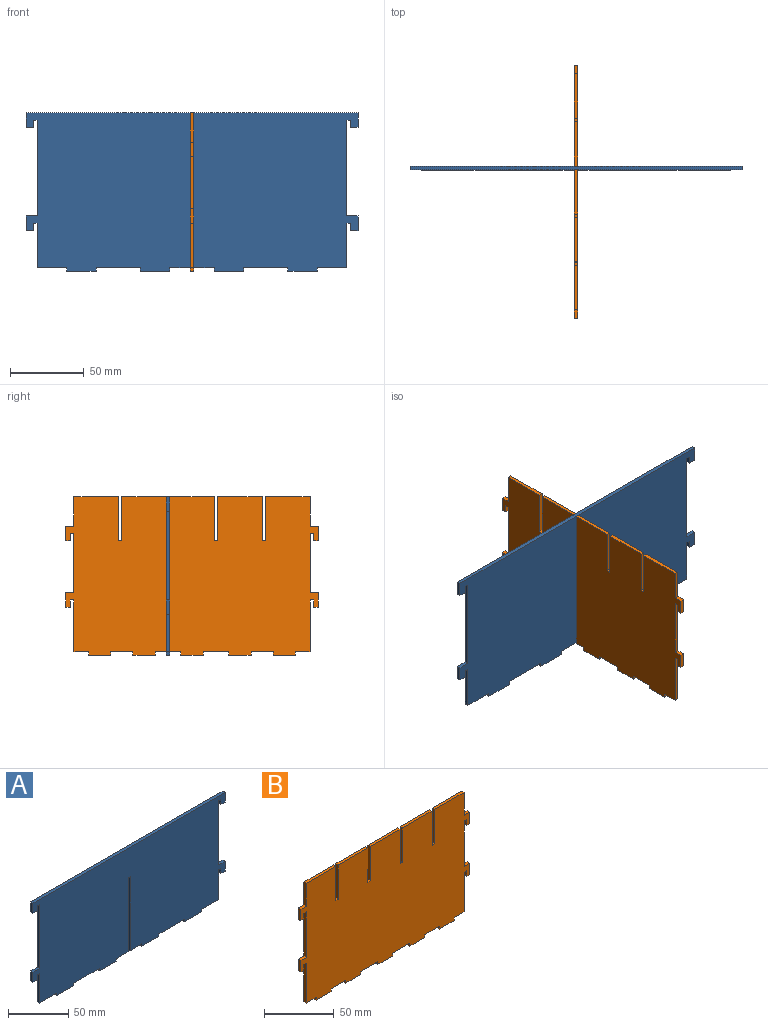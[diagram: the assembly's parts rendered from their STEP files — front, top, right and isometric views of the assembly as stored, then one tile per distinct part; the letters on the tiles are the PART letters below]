
ASSEMBLY  parts=2 mates=1
PART A: 46 faces, bbox 225x2.5x107.5 mm
  f0: plane 75x2.5mm, normal (1,0,0), area 187.5mm2, adj f1,f43,f44,f45
  f1: plane 2.5x2.5mm, normal (0,0,-1), area 6.2mm2, adj f0,f2,f44,f45
  f2: plane 75x2.5mm, normal (-1,0,0), area 187.5mm2, adj f1,f3,f44,f45
  f3: plane 13.75x2.5mm, normal (0,0,-1), area 34.4mm2, adj f2,f4,f44,f45
  f4: plane 2.5x2.5mm, normal (-1,0,0), area 6.2mm2, adj f3,f5,f44,f45
  f5: plane 20x2.5mm, normal (0,0,-1), area 50mm2, adj f4,f6,f44,f45
  f6: plane 2.5x2.5mm, normal (1,0,0), area 6.2mm2, adj f5,f7,f44,f45
  f7: plane 30x2.5mm, normal (0,0,-1), area 75mm2, adj f6,f8,f44,f45
  f8: plane 2.5x2.5mm, normal (-1,0,0), area 6.2mm2, adj f7,f9,f44,f45
  f9: plane 20x2.5mm, normal (0,0,-1), area 50mm2, adj f8,f10,f44,f45
  f10: plane 2.5x2.5mm, normal (1,0,0), area 6.2mm2, adj f9,f11,f44,f45
  f11: plane 20x2.5mm, normal (0,0,-1), area 50mm2, adj f10,f12,f44,f45
  f12: plane 30x2.5mm, normal (1,0,0), area 75mm2, adj f11,f13,f44,f45
  f13: plane 2.5x2.5mm, normal (0,0,-1), area 6.3mm2, adj f12,f14,f44,f45
  f14: plane 5x2.5mm, normal (-1,0,0), area 12.5mm2, adj f13,f15,f44,f45
  f15: plane 5x2.5mm, normal (0,0,-1), area 12.5mm2, adj f14,f16,f44,f45
  f16: plane 10x2.5mm, normal (1,0,0), area 25mm2, adj f15,f17,f44,f45
  f17: plane 7.5x2.5mm, normal (0,0,1), area 18.8mm2, adj f16,f18,f44,f45
  f18: plane 65x2.5mm, normal (1,0,0), area 162.5mm2, adj f17,f19,f44,f45
  f19: plane 2.5x2.5mm, normal (0,0,-1), area 6.3mm2, adj f18,f20,f44,f45
  f20: plane 5x2.5mm, normal (-1,0,0), area 12.5mm2, adj f19,f21,f44,f45
  f21: plane 5x2.5mm, normal (0,0,-1), area 12.5mm2, adj f20,f22,f44,f45
  f22: plane 10x2.5mm, normal (1,0,0), area 25mm2, adj f21,f23,f44,f45
  f23: plane 225x2.5mm, normal (0,0,1), area 562.5mm2, adj f22,f24,f44,f45
  f24: plane 10x2.5mm, normal (-1,0,0), area 25mm2, adj f23,f25,f44,f45
  f25: plane 5x2.5mm, normal (0,0,-1), area 12.5mm2, adj f24,f26,f44,f45
  f26: plane 5x2.5mm, normal (1,0,0), area 12.5mm2, adj f25,f27,f44,f45
  f27: plane 2.5x2.5mm, normal (0,0,-1), area 6.3mm2, adj f26,f28,f44,f45
  f28: plane 65x2.5mm, normal (-1,0,0), area 162.5mm2, adj f27,f29,f44,f45
  f29: plane 7.5x2.5mm, normal (0,0,1), area 18.8mm2, adj f28,f30,f44,f45
  f30: plane 10x2.5mm, normal (-1,0,0), area 25mm2, adj f29,f31,f44,f45
  f31: plane 5x2.5mm, normal (0,0,-1), area 12.5mm2, adj f30,f32,f44,f45
  f32: plane 5x2.5mm, normal (1,0,0), area 12.5mm2, adj f31,f33,f44,f45
  f33: plane 2.5x2.5mm, normal (0,0,-1), area 6.3mm2, adj f32,f34,f44,f45
  f34: plane 30x2.5mm, normal (-1,0,0), area 75mm2, adj f33,f35,f44,f45
  f35: plane 20x2.5mm, normal (0,0,-1), area 50mm2, adj f34,f36,f44,f45
  f36: plane 2.5x2.5mm, normal (-1,0,0), area 6.3mm2, adj f35,f37,f44,f45
  f37: plane 20x2.5mm, normal (0,0,-1), area 50mm2, adj f36,f38,f44,f45
  f38: plane 2.5x2.5mm, normal (1,0,0), area 6.2mm2, adj f37,f39,f44,f45
  f39: plane 30x2.5mm, normal (0,0,-1), area 75mm2, adj f38,f40,f44,f45
  f40: plane 2.5x2.5mm, normal (-1,0,0), area 6.2mm2, adj f39,f41,f44,f45
  f41: plane 20x2.5mm, normal (0,0,-1), area 50mm2, adj f40,f42,f44,f45
  f42: plane 2.5x2.5mm, normal (1,0,0), area 6.2mm2, adj f41,f43,f44,f45
  f43: plane 13.75x2.5mm, normal (0,0,-1), area 34.4mm2, adj f0,f42,f44,f45
  f44: plane 225x107.5mm, normal (0,-1,0), area 22312.5mm2, adj f0,f1,f2,f3,f4,f5,f6,f7
  f45: plane 225x107.5mm, normal (0,1,0), area 22312.5mm2, adj f0,f1,f2,f3,f4,f5,f6,f7
PART B: 66 faces, bbox 171x2.5x107.5 mm
  f0: plane 15x2.5mm, normal (0,0,-1), area 37.5mm2, adj f1,f63,f64,f65
  f1: plane 2.5x2.5mm, normal (1,0,0), area 6.2mm2, adj f0,f2,f64,f65
  f2: plane 17.5x2.5mm, normal (0,0,-1), area 43.8mm2, adj f1,f3,f64,f65
  f3: plane 2.5x2.5mm, normal (-1,0,0), area 6.3mm2, adj f2,f4,f64,f65
  f4: plane 15x2.5mm, normal (0,0,-1), area 37.5mm2, adj f3,f5,f64,f65
  f5: plane 2.5x2.5mm, normal (1,0,0), area 6.2mm2, adj f4,f6,f64,f65
  f6: plane 15x2.5mm, normal (0,0,-1), area 37.5mm2, adj f5,f7,f64,f65
  f7: plane 2.5x2.5mm, normal (-1,0,0), area 6.2mm2, adj f6,f8,f64,f65
  f8: plane 15x2.5mm, normal (0,0,-1), area 37.5mm2, adj f7,f9,f64,f65
  f9: plane 2.5x2.5mm, normal (1,0,0), area 6.2mm2, adj f8,f10,f64,f65
  f10: plane 10x2.5mm, normal (0,0,-1), area 25mm2, adj f9,f11,f64,f65
  f11: plane 35x2.5mm, normal (1,0,0), area 87.5mm2, adj f10,f12,f64,f65
  f12: plane 2.5x2.5mm, normal (0,0,-1), area 6.3mm2, adj f11,f13,f64,f65
  f13: plane 5x2.5mm, normal (-1,0,0), area 12.5mm2, adj f12,f14,f64,f65
  f14: plane 3x2.5mm, normal (0,0,-1), area 7.5mm2, adj f13,f15,f64,f65
  f15: plane 10x2.5mm, normal (1,0,0), area 25mm2, adj f14,f16,f64,f65
  f16: plane 5.5x2.5mm, normal (0,0,1), area 13.8mm2, adj f15,f17,f64,f65
  f17: plane 40x2.5mm, normal (1,0,0), area 100mm2, adj f16,f18,f64,f65
  f18: plane 2.5x2.5mm, normal (0,0,-1), area 6.3mm2, adj f17,f19,f64,f65
  f19: plane 5x2.5mm, normal (-1,0,0), area 12.5mm2, adj f18,f20,f64,f65
  f20: plane 3x2.5mm, normal (0,0,-1), area 7.5mm2, adj f19,f21,f64,f65
  f21: plane 10x2.5mm, normal (1,0,0), area 25mm2, adj f20,f22,f64,f65
  f22: plane 5.5x2.5mm, normal (0,0,1), area 13.8mm2, adj f21,f23,f64,f65
  f23: plane 20x2.5mm, normal (1,0,0), area 50mm2, adj f22,f24,f64,f65
  f24: plane 30x2.5mm, normal (0,0,1), area 75mm2, adj f23,f25,f64,f65
  f25: plane 30x2.5mm, normal (-1,0,0), area 75mm2, adj f24,f26,f64,f65
  f26: plane 2.5x2.5mm, normal (0,0,1), area 6.3mm2, adj f25,f27,f64,f65
  f27: plane 30x2.5mm, normal (1,0,0), area 75mm2, adj f26,f28,f64,f65
  f28: plane 30x2.5mm, normal (0,0,1), area 75mm2, adj f27,f29,f64,f65
  f29: plane 30x2.5mm, normal (-1,0,0), area 75mm2, adj f28,f30,f64,f65
  f30: plane 2.5x2.5mm, normal (0,0,1), area 6.3mm2, adj f29,f31,f64,f65
  f31: plane 30x2.5mm, normal (1,0,0), area 75mm2, adj f30,f32,f64,f65
  f32: plane 30x2.5mm, normal (0,0,1), area 75mm2, adj f31,f33,f64,f65
  f33: plane 30x2.5mm, normal (-1,0,0), area 75mm2, adj f32,f34,f64,f65
  f34: plane 2.5x2.5mm, normal (0,0,1), area 6.3mm2, adj f33,f35,f64,f65
  f35: plane 30x2.5mm, normal (1,0,0), area 75mm2, adj f34,f36,f64,f65
  f36: plane 30x2.5mm, normal (0,0,1), area 75mm2, adj f35,f37,f64,f65
  f37: plane 30x2.5mm, normal (-1,0,0), area 75mm2, adj f36,f38,f64,f65
  f38: plane 2.5x2.5mm, normal (0,0,1), area 6.3mm2, adj f37,f39,f64,f65
  f39: plane 30x2.5mm, normal (1,0,0), area 75mm2, adj f38,f40,f64,f65
  f40: plane 30x2.5mm, normal (0,0,1), area 75mm2, adj f39,f41,f64,f65
  f41: plane 20x2.5mm, normal (-1,0,0), area 50mm2, adj f40,f42,f64,f65
  f42: plane 5.5x2.5mm, normal (0,0,1), area 13.8mm2, adj f41,f43,f64,f65
  f43: plane 10x2.5mm, normal (-1,0,0), area 25mm2, adj f42,f44,f64,f65
  f44: plane 3x2.5mm, normal (0,0,-1), area 7.5mm2, adj f43,f45,f64,f65
  f45: plane 5x2.5mm, normal (1,0,0), area 12.5mm2, adj f44,f46,f64,f65
  f46: plane 2.5x2.5mm, normal (0,0,-1), area 6.3mm2, adj f45,f47,f64,f65
  f47: plane 40x2.5mm, normal (-1,0,0), area 100mm2, adj f46,f48,f64,f65
  f48: plane 5.5x2.5mm, normal (0,0,1), area 13.8mm2, adj f47,f49,f64,f65
  f49: plane 10x2.5mm, normal (-1,0,0), area 25mm2, adj f48,f50,f64,f65
  f50: plane 3x2.5mm, normal (0,0,-1), area 7.5mm2, adj f49,f51,f64,f65
  f51: plane 5x2.5mm, normal (1,0,0), area 12.5mm2, adj f50,f52,f64,f65
  f52: plane 2.5x2.5mm, normal (0,0,-1), area 6.3mm2, adj f51,f53,f64,f65
  f53: plane 35x2.5mm, normal (-1,0,0), area 87.5mm2, adj f52,f54,f64,f65
  f54: plane 10x2.5mm, normal (0,0,-1), area 25mm2, adj f53,f55,f64,f65
  f55: plane 2.5x2.5mm, normal (-1,0,0), area 6.2mm2, adj f54,f56,f64,f65
  f56: plane 15x2.5mm, normal (0,0,-1), area 37.5mm2, adj f55,f57,f64,f65
  f57: plane 2.5x2.5mm, normal (1,0,0), area 6.2mm2, adj f56,f58,f64,f65
  f58: plane 15x2.5mm, normal (0,0,-1), area 37.5mm2, adj f57,f59,f64,f65
  f59: plane 2.5x2.5mm, normal (-1,0,0), area 6.2mm2, adj f58,f60,f64,f65
  f60: plane 15x2.5mm, normal (0,0,-1), area 37.5mm2, adj f59,f61,f64,f65
  f61: plane 2.5x2.5mm, normal (1,0,0), area 6.2mm2, adj f60,f62,f64,f65
  f62: plane 17.5x2.5mm, normal (0,0,-1), area 43.8mm2, adj f61,f63,f64,f65
  f63: plane 2.5x2.5mm, normal (-1,0,0), area 6.2mm2, adj f0,f62,f64,f65
  f64: plane 171x107.5mm, normal (0,-1,0), area 16857.5mm2, adj f0,f1,f2,f3,f4,f5,f6,f7
  f65: plane 171x107.5mm, normal (0,1,0), area 16857.5mm2, adj f0,f1,f2,f3,f4,f5,f6,f7
PLACE A t=(-16.42,-85.57,-29.41)mm
PLACE B rot(axis=(0,0,-1),90deg) t=(-15.17,-103.07,-29.41)mm
MATE fastened B.f34 <-> A.f1  axis (0,0,1) through (-16.42,-86.82,45.59)mm
